# Revit family: Hekatron_Feststellanlagen_THM 439-485_DE_22.01
name_source: partatom
category: Brandmelder
revit_build: Autodesk Revit 2018 (Build: 20190510_1515(x64)
units: mm (PartAtom-declared; Revit-internal decimal feet)

## family parameters
Basisbauteil = Fläche
Beim Laden mit Abzugskörper schneiden = Nein
Bemaßung runder Anschluss = Durchmesser verwenden
Beschriftungsausrichtung beibehalten = Ja
Gemeinsam genutzt = Nein
OmniClass-Nummer = 23.85.30.21
OmniClass-Titel = Environmental Detection/Registration
Raumberechnungspunkt = Nein
Teiletyp = Normal

## types (1)
- THM 439/485
    Bauartgenehmigungen = Z-6.500-2325, Z-6.500-2340, Z-6.500-2359, Z-6.500-2393, Z-6.500-2394, Z-6.500-2414, Z-6.500-2415, Z-6.500-2419, Z-6.500-2441, Z-6.500-2442, Z-6.500-2411, Z-6.500-2444, Z-6.500-2436, Z-6.500-2450, Z-6.500-2451, Z-6.500-2452, Z-6.500-2457, Z-6.500-2515
    Beschreibung = Türhaftmagnet in runder Bauform mit verdeckten Anschlussklemmen. Der Kopf ist dreh- und schwenkbar. Länge 485 mm. Mit Verpolschutz und Löschdiode. Passend zur Ankerplatte ASS 55.
    Betriebsspannung = 24 V DC
    Breite (mm) = 485.0
    EG-Konformitätszertifikat / Zertifikat der Leistungsbeständigkeit = 0786-CPR-21391
    Farbe = Metall
    Hersteller = Hekatron
    Höhe (mm) = 80.0
    Kabeleinführung = unten, hinten
    Leistungserklärung (DoP) = CPR-31-13-500-de-en
    Link zu Ausschreibungstext = https://www.meinhplus.de
    Link zu Produktinformation = https://www.hekatron-planungstools.de
    Link zu ausschreiben.de = http://www.ausschreiben.de
    Material = Metall
    Modell = THM 439/485
    Montageart = Aufputz
    Schutzart = IP 40
    Stromaufnahme = max. 63mA
    Tiefe (mm) = 90.0
    Typenkommentare = Türhaftmagnet THM 439-485
    UB A&S Artikel Nummer = 6500129
    URL = https://www.hekatron-brandschutz.de
    Version des BIM Objektes = 22.01
    Vorgabe-Ansicht = 1200 mm
    Zulässige Umgebungstemperatur = 0 °C bis +50 °C

## geometry (parser evidence)
native form markers: Sweep x2
no freeform markers — native parametric forms only
